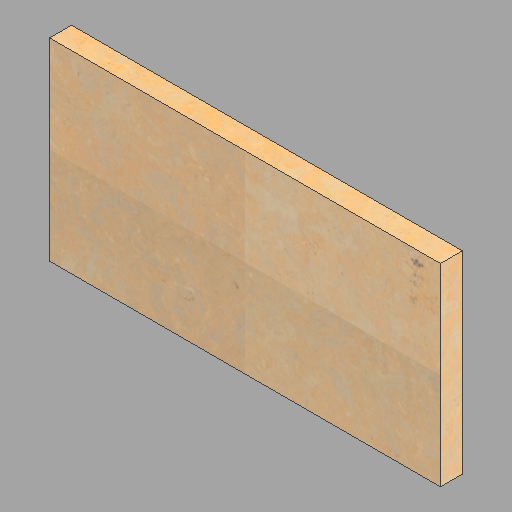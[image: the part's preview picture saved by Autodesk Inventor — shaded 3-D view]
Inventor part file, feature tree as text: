
AUTODESK INVENTOR PART (.ipt)
format: ipt  version: 2023 (Build 270158000, 158)  size: 289,792 bytes
history: native  units: in
note: dims shown in document units (in); Inventor stores cm internally (conversion verified against a paired STEP export)
features: extrude x1, sketch x1
ambient origin geometry x8: Origin, YZ Plane, XZ Plane, XY Plane, X Axis, Y Axis, Z Axis, Center Point
bodies: Solid1 (feature_tree)
feature tree (2):
  extrude  "Extrusion1"  Depth=17.625in
  sketch  "Sketch1"  dims[d0=35.625in d1=17.625in d2=2.0in d3=0.0in]
